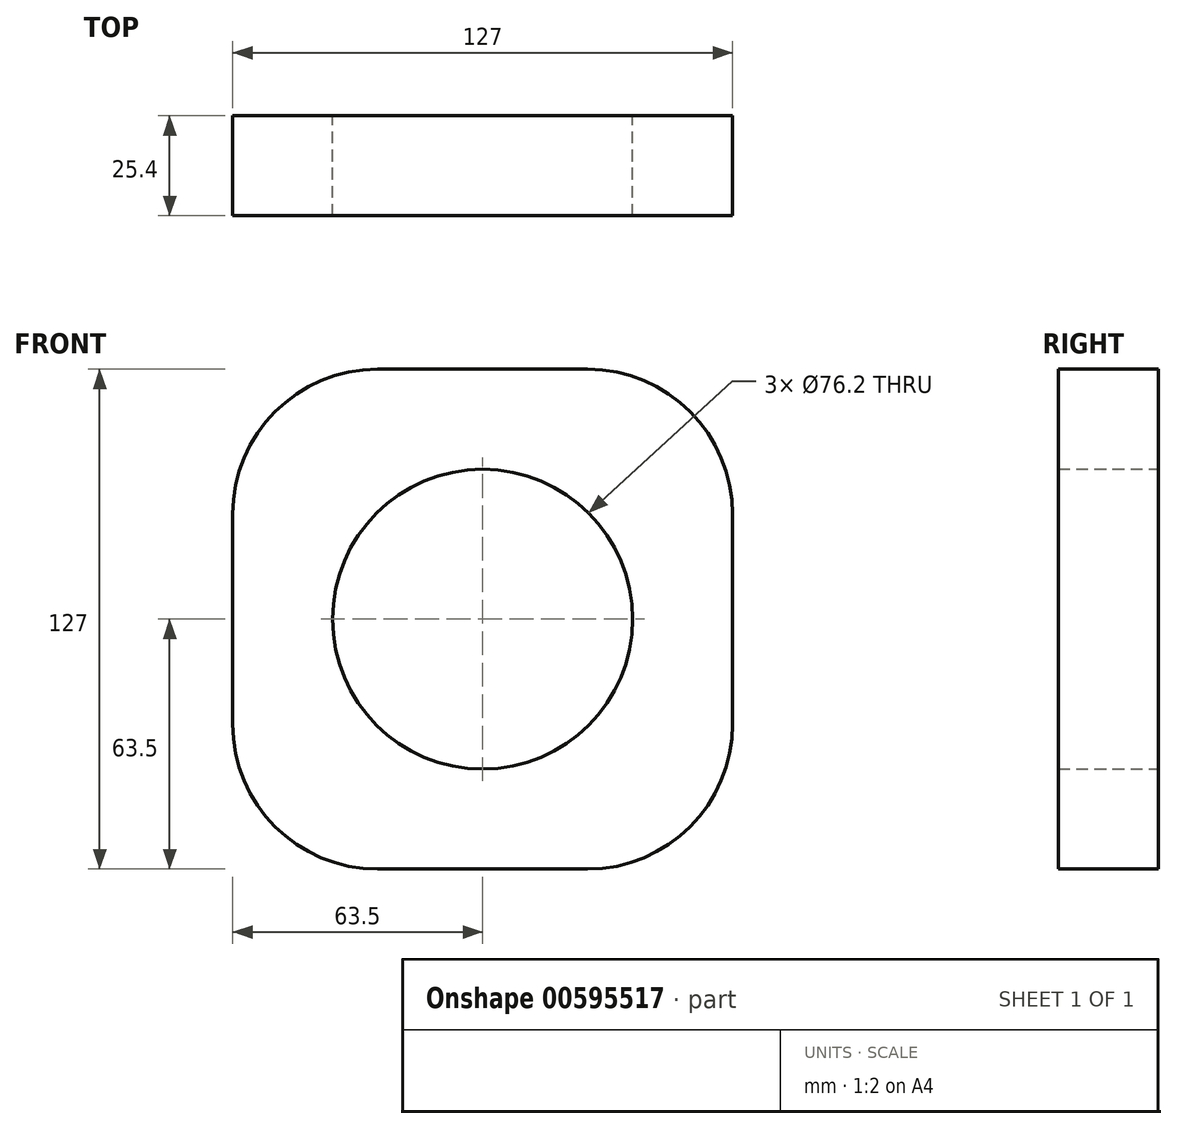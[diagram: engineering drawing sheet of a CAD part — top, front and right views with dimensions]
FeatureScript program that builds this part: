
annotation { "Feature Type Name" : "Feature", "Feature Type Description" : "" }
export const myFeature = defineFeature(function(context is Context, id is Id, definition is map)
    precondition{}
    {
        {
            var Q0;
            Q0=qCreatedBy(makeId("Front.planeOp"),FACE);
            var sketch = newSketch(context, id + "F0", { "sketchPlane" : qUnion([Q0])});
            skLineSegment(sketch, "E0.bottom", {"start": v(-26.68, 63.5) * mm, "end": v(26.67, 63.5) * mm});
            skLineSegment(sketch, "E0.top", {"start": v(-26.67, -63.5) * mm, "end": v(26.68, -63.5) * mm});
            skLineSegment(sketch, "E0.left", {"start": v(-63.5, 26.68) * mm, "end": v(-63.5, -26.67) * mm});
            skLineSegment(sketch, "E0.right", {"start": v(63.5, 26.67) * mm, "end": v(63.5, -26.68) * mm});
            skPoint(sketch, "E0.middle", {"position": v(0, 0) * mm});
            skPoint(sketch, "E1.visualSharp", {"position": v(-63.5, 63.5) * mm});
            skArc(sketch, "E1.filletArc", {"start": v(-26.68, 63.5) * mm, "mid": v(-52.71, 52.71) * mm, "end": v(-63.5, 26.68) * mm});
            skPoint(sketch, "E2.visualSharp", {"position": v(63.5, 63.5) * mm});
            skArc(sketch, "E2.filletArc", {"start": v(63.5, 26.67) * mm, "mid": v(52.71, 52.71) * mm, "end": v(26.67, 63.5) * mm});
            skPoint(sketch, "E3.visualSharp", {"position": v(-63.5, -63.5) * mm});
            skArc(sketch, "E3.filletArc", {"start": v(-63.5, -26.67) * mm, "mid": v(-52.71, -52.71) * mm, "end": v(-26.67, -63.5) * mm});
            skPoint(sketch, "E4.visualSharp", {"position": v(63.5, -63.5) * mm});
            skArc(sketch, "E4.filletArc", {"start": v(26.68, -63.5) * mm, "mid": v(52.71, -52.71) * mm, "end": v(63.5, -26.68) * mm});
            skCircle(sketch, "E5", {"center": v(0, 0) * mm, "radius": 38.1 * mm});
            skSolve(sketch);
        }
        {
            var Q0;
            Q0=sQuery(id+"F0.wireOp",EDGE,"E0.left");
            extrude(context, id + "F1", {"bodyType" : ToolBodyType.SURFACE, "surfaceEntities" : qUnion([Q0]), "depth" : 25.4 * mm, "offsetDistance" : 25.4 * mm});
        }
        {
            var Q0;
            {var subQ0=sQuery(id+"F0.wireOp",EDGE,"E3.filletArc");Q0=makeQuery(id+"F0.imprint","IMPRINT",FACE,{"disambiguationData":[TD([[makeQuery(id+"F0.imprint","IMPRINT",EDGE,{"derivedFrom":subQ0}),1.0]])]});}
            extrude(context, id + "F2", {"entities" : qUnion([Q0]), "depth" : 25.4 * mm, "offsetDistance" : 25.4 * mm});
        }
        {
            var Q0;
            {var subQ0=sQuery(id+"F0.wireOp",EDGE,"E1.filletArc");Q0=makeQuery(id+"F0.imprint","IMPRINT",FACE,{"disambiguationData":[TD([[makeQuery(id+"F0.imprint","IMPRINT",EDGE,{"derivedFrom":subQ0}),1.0]])]});}
            extrude(context, id + "F3", {"entities" : qUnion([Q0]), "depth" : 25.4 * mm, "offsetDistance" : 25.4 * mm});
        }
        {
            var Q0;
            {var subQ0=sQuery(id+"F0.wireOp",EDGE,"E2.filletArc");Q0=makeQuery(id+"F0.imprint","IMPRINT",FACE,{"disambiguationData":[TD([[makeQuery(id+"F0.imprint","IMPRINT",EDGE,{"derivedFrom":subQ0}),1.0]])]});}
            extrude(context, id + "F4", {"entities" : qUnion([Q0]), "depth" : 25.4 * mm, "offsetDistance" : 25.4 * mm});
        }
    });
